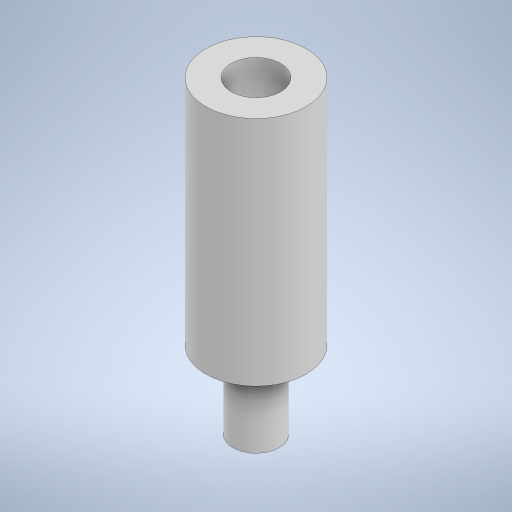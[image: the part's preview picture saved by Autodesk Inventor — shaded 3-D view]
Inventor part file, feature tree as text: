
AUTODESK INVENTOR PART (.ipt)
format: ipt  version: 2024.2 (Build 282272000, 272)  size: 239,104 bytes
history: native  units: mm
features: extrude x3, sketch x3
ambient origin geometry x8: Origin, YZ Plane, XZ Plane, XY Plane, X Axis, Y Axis, Z Axis, Center Point
bodies: Solid1 (feature_tree)
feature tree (6):
  extrude  "Extrusion1"  Depth=5.0mm TaperAngle=0.0deg
  extrude  "Extrusion2"  Depth=15.0mm TaperAngle=0.0deg
  extrude  "Extrusion3"  Depth=2.5mm TaperAngle=0.0deg
  sketch  "Sketch1"  dims[d0=3.0mm d1=5.0mm d2=0.0mm]
  sketch  "Sketch2"  dims[d3=6.5mm d4=15.0mm d5=0.0mm]
  sketch  "Sketch3"  dims[d6=3.2mm d7=2.5mm d8=0.0mm]
